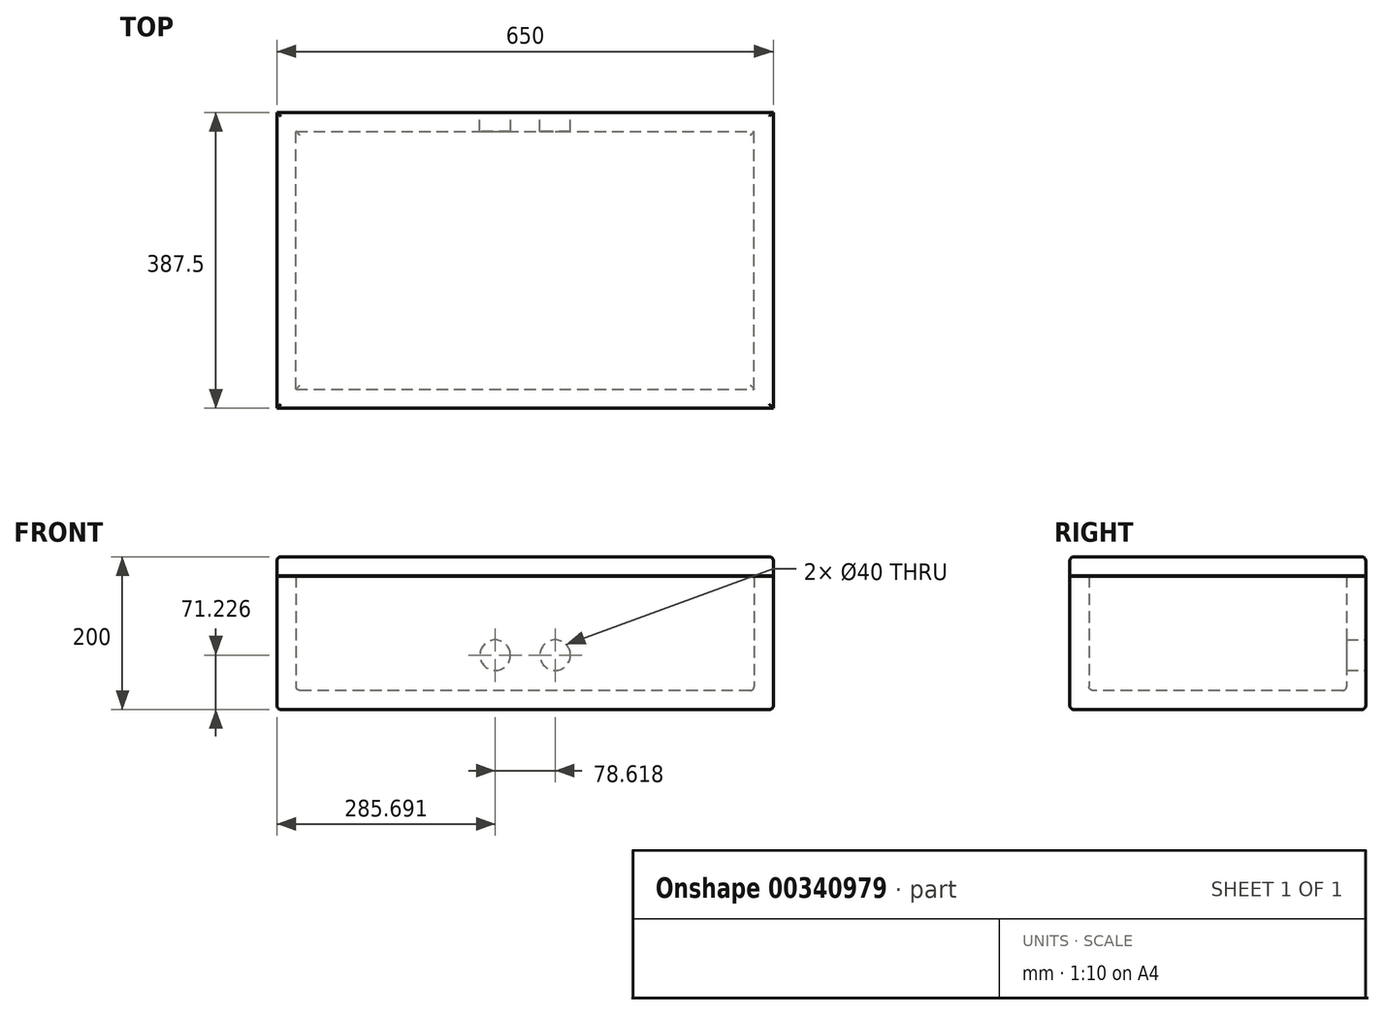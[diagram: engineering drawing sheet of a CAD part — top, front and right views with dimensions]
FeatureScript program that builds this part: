
annotation { "Feature Type Name" : "Feature", "Feature Type Description" : "" }
export const myFeature = defineFeature(function(context is Context, id is Id, definition is map)
    precondition{}
    {
        {
            var Q0;
            Q0=qCreatedBy(makeId("Top.planeOp"),FACE);
            var sketch = newSketch(context, id + "F0", { "sketchPlane" : qUnion([Q0])});
            skLineSegment(sketch, "E0.bottom", {"start": v(325, 193.75) * mm, "end": v(-325, 193.75) * mm});
            skLineSegment(sketch, "E0.top", {"start": v(325, -193.75) * mm, "end": v(-325, -193.75) * mm});
            skLineSegment(sketch, "E0.left", {"start": v(325, 193.75) * mm, "end": v(325, -193.75) * mm});
            skLineSegment(sketch, "E0.right", {"start": v(-325, 193.75) * mm, "end": v(-325, -193.75) * mm});
            skPoint(sketch, "E0.middle", {"position": v(0, 0) * mm});
            skSolve(sketch);
        }
        {
            var Q0;
            Q0=makeQuery(id+"F0.imprint","IMPRINT",FACE,{"disambiguationData":[TD([[makeQuery(id+"F0.imprint","IMPRINT",EDGE,{"derivedFrom":sQuery(id+"F0.wireOp",EDGE,"E0.bottom")}),1.0]])]});
            extrude(context, id + "F1", {"entities" : qUnion([Q0]), "depth" : 200 * mm});
        }
        {
            var Q0;
            Q0=makeQuery(id+"F1.opExtrude","CAP_FACE",FACE,{"disambiguationData":[OSD([sQuery(id+"F0.wireOp",EDGE,"E0.bottom"),sQuery(id+"F0.wireOp",EDGE,"E0.top"),sQuery(id+"F0.wireOp",EDGE,"E0.left"),sQuery(id+"F0.wireOp",EDGE,"E0.right")])],"isStart":false});
            shell(context, id + "F2", {"entities" : qUnion([Q0]), "thickness" : 25 * mm});
        }
        {
            var Q0;
            Q0=makeQuery(id+"F1.opExtrude","SWEPT_FACE",FACE,{"disambiguationData":[OSD([sQuery(id+"F0.wireOp",EDGE,"E0.bottom")])]});
            var sketch = newSketch(context, id + "F3", { "sketchPlane" : qUnion([Q0])});
            skLineSegment(sketch, "E1", {"start": v(-325.08, 71.23) * mm, "end": v(-39.3, 71.23) * mm, "construction": true});
            skLineSegment(sketch, "E2", {"start": v(39.3, 71.23) * mm, "end": v(325.08, 71.23) * mm, "construction": true});
            skLineSegment(sketch, "E3", {"start": v(0, 0) * mm, "end": v(0, 200) * mm, "construction": true});
            skLineSegment(sketch, "E4", {"start": v(0, 71.23) * mm, "end": v(39.3, 71.23) * mm, "construction": true});
            skLineSegment(sketch, "E5", {"start": v(0, 71.23) * mm, "end": v(-39.3, 71.23) * mm, "construction": true});
            skCircle(sketch, "E6", {"center": v(-39.3, 71.23) * mm, "radius": 20 * mm});
            skCircle(sketch, "E7", {"center": v(39.3, 71.23) * mm, "radius": 20 * mm});
            skSolve(sketch);
        }
        {
            var Q0;
            Q0=makeQuery(id+"F3.imprint","IMPRINT",FACE,{"disambiguationData":[TD([[makeQuery(id+"F3.imprint","IMPRINT",EDGE,{"derivedFrom":sQuery(id+"F3.wireOp",EDGE,"E6")}),1.0]])]});
            var Q1;
            Q1=makeQuery(id+"F3.imprint","IMPRINT",FACE,{"disambiguationData":[TD([[makeQuery(id+"F3.imprint","IMPRINT",EDGE,{"derivedFrom":sQuery(id+"F3.wireOp",EDGE,"E7")}),1.0]])]});
            extrude(context, id + "F4", {"entities" : qUnion([Q0, Q1]), "operationType" : NewBodyOperationType.REMOVE, "oppositeDirection" : true, "depth" : 25 * mm});
        }
        {
            var Q0;
            Q0=makeQuery(id+"F2.opShell","OFFSET_FACE",FACE,{"disambiguationData":[OSD([sQuery(id+"F0.wireOp",EDGE,"E0.bottom"),sQuery(id+"F0.wireOp",EDGE,"E0.top"),sQuery(id+"F0.wireOp",EDGE,"E0.left"),sQuery(id+"F0.wireOp",EDGE,"E0.right")])]});
            var Q1;
            Q1=makeQuery(id+"F1.opExtrude","CAP_FACE",FACE,{"disambiguationData":[OSD([sQuery(id+"F0.wireOp",EDGE,"E0.bottom"),sQuery(id+"F0.wireOp",EDGE,"E0.top"),sQuery(id+"F0.wireOp",EDGE,"E0.left"),sQuery(id+"F0.wireOp",EDGE,"E0.right")])],"isStart":false});
            var Q2;
            Q2=makeQuery(id+"F1.opExtrude","CAP_FACE",FACE,{"disambiguationData":[OSD([sQuery(id+"F0.wireOp",EDGE,"E0.bottom"),sQuery(id+"F0.wireOp",EDGE,"E0.top"),sQuery(id+"F0.wireOp",EDGE,"E0.left"),sQuery(id+"F0.wireOp",EDGE,"E0.right")])],"isStart":true});
            fillet(context, id + "F5", {"entities" : qUnion([Q0, Q1, Q2]), "radius" : 5 * mm, "tangentPropagation" : true, "allowEdgeOverflow" : false});
        }
        {
            var Q0;
            Q0=makeQuery(id+"F1.opExtrude","SWEPT_FACE",FACE,{"disambiguationData":[OSD([sQuery(id+"F0.wireOp",EDGE,"E0.top")])]});
            var sketch = newSketch(context, id + "F6", { "sketchPlane" : qUnion([Q0])});
            skLineSegment(sketch, "E8.bottom", {"start": v(-353.59, 174.9) * mm, "end": v(402.97, 174.9) * mm});
            skLineSegment(sketch, "E8.top", {"start": v(-353.59, 175) * mm, "end": v(402.97, 175) * mm});
            skLineSegment(sketch, "E8.left", {"start": v(-353.59, 174.9) * mm, "end": v(-353.59, 175) * mm});
            skLineSegment(sketch, "E8.right", {"start": v(402.97, 174.9) * mm, "end": v(402.97, 175) * mm});
            skSolve(sketch);
        }
        {
            var Q0;
            Q0 = qSketchRegion(id + "F6", true);
            extrude(context, id + "F7", {"entities" : qUnion([Q0]), "operationType" : NewBodyOperationType.REMOVE, "oppositeDirection" : true, "depth" : 500 * mm});
        }
        {
            var Q0;
            Q0=makeQuery(id+"F1.opExtrude","CAP_FACE",FACE,{"disambiguationData":[OSD([sQuery(id+"F0.wireOp",EDGE,"E0.bottom"),sQuery(id+"F0.wireOp",EDGE,"E0.top"),sQuery(id+"F0.wireOp",EDGE,"E0.left"),sQuery(id+"F0.wireOp",EDGE,"E0.right")])],"isStart":false});
            var sketch = newSketch(context, id + "F8", { "sketchPlane" : qUnion([Q0])});
            skLineSegment(sketch, "E9.bottom", {"start": v(-305, 173.75) * mm, "end": v(305, 173.75) * mm});
            skLineSegment(sketch, "E9.top", {"start": v(-305, -173.75) * mm, "end": v(305, -173.75) * mm});
            skLineSegment(sketch, "E9.left", {"start": v(-305, 173.75) * mm, "end": v(-305, -173.75) * mm});
            skLineSegment(sketch, "E9.right", {"start": v(305, 173.75) * mm, "end": v(305, -173.75) * mm});
            skSolve(sketch);
        }
        {
            var Q0;
            Q0 = qSketchRegion(id + "F8", true);
            extrude(context, id + "F9", {"entities" : qUnion([Q0]), "operationType" : NewBodyOperationType.ADD, "oppositeDirection" : true, "depth" : 25 * mm});
        }
    });
